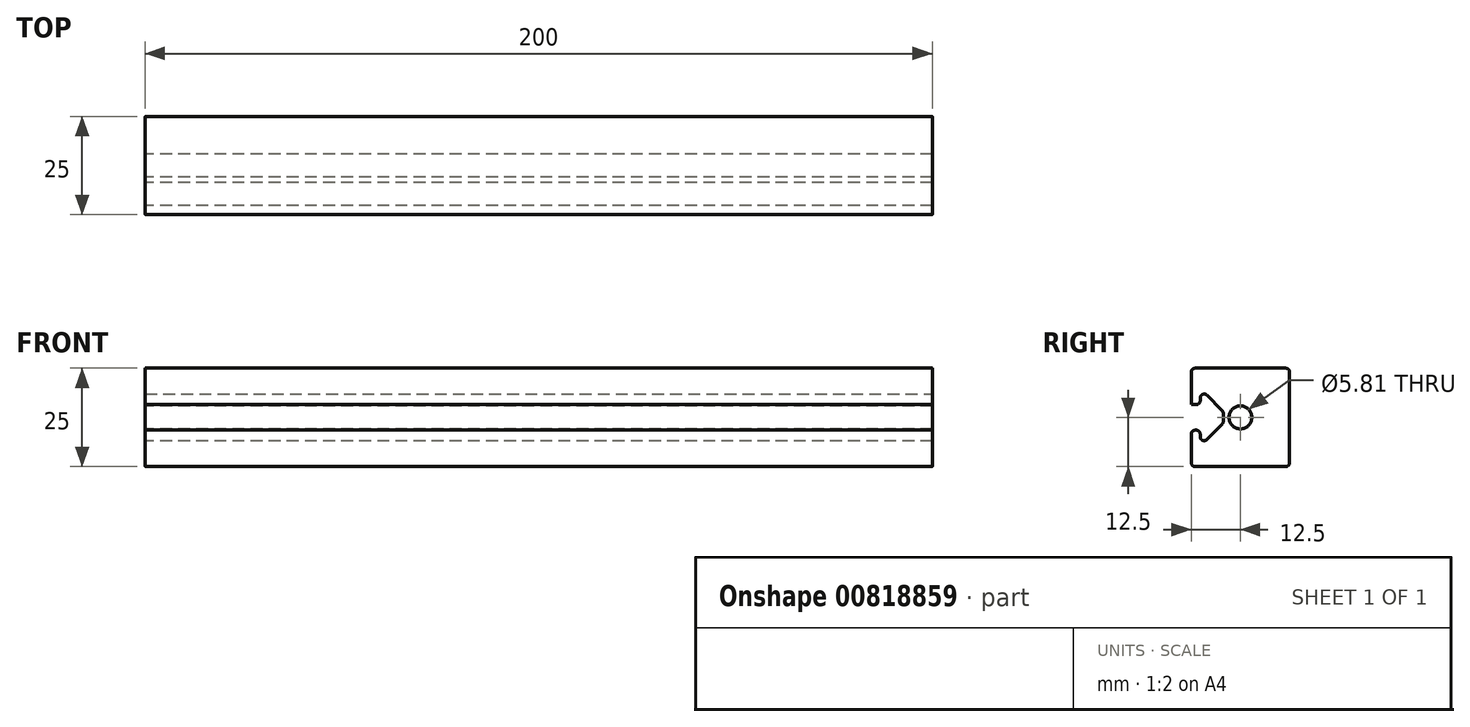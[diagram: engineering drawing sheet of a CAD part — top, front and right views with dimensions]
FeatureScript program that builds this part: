
annotation { "Feature Type Name" : "Feature", "Feature Type Description" : "" }
export const myFeature = defineFeature(function(context is Context, id is Id, definition is map)
    precondition{}
    {
        {
            var Q0;
            Q0=qCreatedBy(makeId("Right.planeOp"),FACE);
            var sketch = newSketch(context, id + "F0", { "sketchPlane" : qUnion([Q0])});
            skLineSegment(sketch, "E0.bottom", {"start": v(-12.5, -25) * mm, "end": v(12.5, -25) * mm});
            skLineSegment(sketch, "E0.top", {"start": v(-12.5, 25) * mm, "end": v(12.5, 25) * mm});
            skLineSegment(sketch, "E0.left", {"start": v(-12.5, -25) * mm, "end": v(-12.5, 25) * mm});
            skLineSegment(sketch, "E0.right", {"start": v(12.5, -25) * mm, "end": v(12.5, 25) * mm});
            skPoint(sketch, "E0.middle", {"position": v(0, 0) * mm});
            skLineSegment(sketch, "E1.bottom", {"start": v(12.5, 15.75) * mm, "end": v(4.38, 15.75) * mm});
            skLineSegment(sketch, "E1.top", {"start": v(12.5, 9.25) * mm, "end": v(4.38, 9.25) * mm});
            skLineSegment(sketch, "E1.left", {"start": v(12.5, 15.75) * mm, "end": v(12.5, 9.25) * mm});
            skLineSegment(sketch, "E1.right", {"start": v(4.38, 15.75) * mm, "end": v(4.38, 9.25) * mm});
            skLineSegment(sketch, "E2.bottom", {"start": v(4.38, 19.85) * mm, "end": v(10.22, 19.85) * mm});
            skLineSegment(sketch, "E2.top", {"start": v(4.38, 5.16) * mm, "end": v(10.22, 5.16) * mm});
            skLineSegment(sketch, "E2.left", {"start": v(4.38, 19.85) * mm, "end": v(4.38, 5.16) * mm});
            skLineSegment(sketch, "E2.right", {"start": v(10.22, 19.85) * mm, "end": v(10.22, 5.16) * mm});
            skPoint(sketch, "E2.middle", {"position": v(7.3, 12.5) * mm});
            skLineSegment(sketch, "E3", {"start": v(7.3, 12.5) * mm, "end": v(12.5, 12.5) * mm});
            skLineSegment(sketch, "E4", {"start": v(0, 25) * mm, "end": v(0, 0) * mm});
            skLineSegment(sketch, "E5", {"start": v(4.38, 14) * mm, "end": v(10.22, 19.85) * mm});
            skLineSegment(sketch, "E6.MirrorCS", {"start": v(4.38, 11) * mm, "end": v(10.22, 5.16) * mm});
            skLineSegment(sketch, "E7", {"start": v(-12.5, 0) * mm, "end": v(12.5, 0) * mm});
            skSolve(sketch);
        }
        {
            var Q0;
            {var subQ5=sQuery(id+"F0.wireOp",EDGE,"E2.right");var subQ6=sQuery(id+"F0.wireOp",EDGE,"E1.bottom");var subQ7=makeQuery(id+"F0.imprint","INTERSECT",VERTEX,{"derivedFrom":[subQ6,subQ5]});Q0=makeQuery(id+"F0.imprint","IMPRINT",FACE,{"disambiguationData":[TD([[makeQuery(id+"F0.imprint","IMPRINT",EDGE,{"disambiguationData":[TD([[subQ7,-1.0]])],"derivedFrom":subQ6}),1.0]])]});}
            var Q1;
            {var subQ0=sQuery(id+"F0.wireOp",EDGE,"E2.right");var subQ1=sQuery(id+"F0.wireOp",EDGE,"E1.top");var subQ2=makeQuery(id+"F0.imprint","INTERSECT",VERTEX,{"derivedFrom":[subQ1,subQ0]});Q1=makeQuery(id+"F0.imprint","IMPRINT",FACE,{"disambiguationData":[TD([[makeQuery(id+"F0.imprint","IMPRINT",EDGE,{"disambiguationData":[TD([[subQ2,-1.0]])],"derivedFrom":subQ1}),1.0]])]});}
            var Q2;
            {var subQ0=sQuery(id+"F0.wireOp",EDGE,"E2.left");var subQ1=sQuery(id+"F0.wireOp",EDGE,"E1.bottom");var subQ2=makeQuery(id+"F0.imprint","INTERSECT",VERTEX,{"derivedFrom":[subQ1,subQ0]});Q2=makeQuery(id+"F0.imprint","IMPRINT",FACE,{"disambiguationData":[TD([[makeQuery(id+"F0.imprint","IMPRINT",EDGE,{"disambiguationData":[TD([[subQ2,1.0]])],"derivedFrom":subQ1}),1.0]])]});}
            var Q3;
            {var subQ5=sQuery(id+"F0.wireOp",EDGE,"E2.bottom");Q3=makeQuery(id+"F0.imprint","IMPRINT",FACE,{"disambiguationData":[TD([[makeQuery(id+"F0.imprint","IMPRINT",EDGE,{"derivedFrom":subQ5}),-1.0]])]});}
            var Q4;
            {var subQ0=sQuery(id+"F0.wireOp",EDGE,"E2.right");var subQ1=sQuery(id+"F0.wireOp",EDGE,"E1.bottom");var subQ2=makeQuery(id+"F0.imprint","INTERSECT",VERTEX,{"derivedFrom":[subQ1,subQ0]});Q4=makeQuery(id+"F0.imprint","IMPRINT",FACE,{"disambiguationData":[TD([[makeQuery(id+"F0.imprint","IMPRINT",EDGE,{"disambiguationData":[TD([[subQ2,-1.0]])],"derivedFrom":subQ1}),-1.0]])]});}
            var Q5;
            {var subQ3=sQuery(id+"F0.wireOp",EDGE,"E2.right");var subQ5=sQuery(id+"F0.wireOp",EDGE,"E3");var subQ7=makeQuery(id+"F0.imprint","INTERSECT",VERTEX,{"derivedFrom":[subQ3,subQ5]});Q5=makeQuery(id+"F0.imprint","IMPRINT",FACE,{"disambiguationData":[TD([[makeQuery(id+"F0.imprint","IMPRINT",EDGE,{"disambiguationData":[TD([[subQ7,1.0]])],"derivedFrom":subQ3}),1.0]])]});}
            var Q6;
            {var subQ3=sQuery(id+"F0.wireOp",EDGE,"E2.right");var subQ5=sQuery(id+"F0.wireOp",EDGE,"E3");var subQ7=makeQuery(id+"F0.imprint","INTERSECT",VERTEX,{"derivedFrom":[subQ3,subQ5]});Q6=makeQuery(id+"F0.imprint","IMPRINT",FACE,{"disambiguationData":[TD([[makeQuery(id+"F0.imprint","IMPRINT",EDGE,{"disambiguationData":[TD([[subQ7,-1.0]])],"derivedFrom":subQ3}),1.0]])]});}
            var Q7;
            {var subQ5=sQuery(id+"F0.wireOp",EDGE,"E2.top");Q7=makeQuery(id+"F0.imprint","IMPRINT",FACE,{"disambiguationData":[TD([[makeQuery(id+"F0.imprint","IMPRINT",EDGE,{"derivedFrom":subQ5}),1.0]])]});}
            var Q8;
            {var subQ0=sQuery(id+"F0.wireOp",EDGE,"E2.left");var subQ1=sQuery(id+"F0.wireOp",EDGE,"E1.top");var subQ2=makeQuery(id+"F0.imprint","INTERSECT",VERTEX,{"derivedFrom":[subQ1,subQ0]});Q8=makeQuery(id+"F0.imprint","IMPRINT",FACE,{"disambiguationData":[TD([[makeQuery(id+"F0.imprint","IMPRINT",EDGE,{"disambiguationData":[TD([[subQ2,1.0]])],"derivedFrom":subQ1}),-1.0]])]});}
            var Q9;
            {var subQ3=sQuery(id+"F0.wireOp",EDGE,"E4");Q9=makeQuery(id+"F0.imprint","IMPRINT",FACE,{"disambiguationData":[TD([[makeQuery(id+"F0.imprint","IMPRINT",EDGE,{"derivedFrom":subQ3}),-1.0]])]});}
            var Q10;
            {var subQ5=sQuery(id+"F0.wireOp",EDGE,"E2.bottom");Q10=makeQuery(id+"F0.imprint","IMPRINT",FACE,{"disambiguationData":[TD([[makeQuery(id+"F0.imprint","IMPRINT",EDGE,{"derivedFrom":subQ5}),1.0]])]});}
            extrude(context, id + "F1", {"entities" : qUnion([Q0, Q1, Q2, Q3, Q4, Q5, Q6, Q7, Q8, Q9, Q10]), "endBound" : BoundingType.SYMMETRIC, "depth" : 200 * mm, "offsetDistance" : 25 * mm});
        }
        {
            var Q0;
            Q0=makeQuery(id+"F1.opExtrude","CAP_FACE",FACE,{"disambiguationData":[OSD([sQuery(id+"F0.wireOp",EDGE,"E0.bottom"),sQuery(id+"F0.wireOp",EDGE,"E0.top"),sQuery(id+"F0.wireOp",EDGE,"E0.left"),sQuery(id+"F0.wireOp",EDGE,"E0.right"),sQuery(id+"F0.wireOp",EDGE,"E1.left")])],"isStart":true});
            var sketch = newSketch(context, id + "F2", { "sketchPlane" : qUnion([Q0])});
            skLineSegment(sketch, "E8.bottom", {"start": v(-12.5, -25) * mm, "end": v(12.5, -25) * mm});
            skLineSegment(sketch, "E8.top", {"start": v(-12.5, 25) * mm, "end": v(12.5, 25) * mm});
            skLineSegment(sketch, "E8.left", {"start": v(-12.5, -25) * mm, "end": v(-12.5, 25) * mm});
            skLineSegment(sketch, "E8.right", {"start": v(12.5, -25) * mm, "end": v(12.5, 25) * mm});
            skPoint(sketch, "E8.middle", {"position": v(0, 0) * mm});
            skLineSegment(sketch, "E9.bottom", {"start": v(12.5, 15.75) * mm, "end": v(4.38, 15.75) * mm});
            skLineSegment(sketch, "E9.top", {"start": v(12.5, 9.25) * mm, "end": v(4.38, 9.25) * mm});
            skLineSegment(sketch, "E9.left", {"start": v(12.5, 15.75) * mm, "end": v(12.5, 9.25) * mm});
            skLineSegment(sketch, "E9.right", {"start": v(4.38, 15.75) * mm, "end": v(4.38, 9.25) * mm});
            skLineSegment(sketch, "E10.bottom", {"start": v(4.38, 19.84) * mm, "end": v(10.22, 19.84) * mm});
            skLineSegment(sketch, "E10.top", {"start": v(4.38, 5.15) * mm, "end": v(10.22, 5.15) * mm});
            skLineSegment(sketch, "E10.left", {"start": v(4.38, 19.84) * mm, "end": v(4.38, 5.15) * mm});
            skLineSegment(sketch, "E10.right", {"start": v(10.22, 19.84) * mm, "end": v(10.22, 5.15) * mm});
            skPoint(sketch, "E10.middle", {"position": v(7.3, 12.5) * mm});
            skLineSegment(sketch, "E11", {"start": v(7.3, 12.5) * mm, "end": v(12.5, 12.5) * mm});
            skLineSegment(sketch, "E12", {"start": v(0, 25) * mm, "end": v(0, 0) * mm});
            skLineSegment(sketch, "E13", {"start": v(4.38, 14) * mm, "end": v(10.22, 19.84) * mm});
            skLineSegment(sketch, "E14.MirrorCS", {"start": v(4.38, 11) * mm, "end": v(10.22, 5.16) * mm});
            skCircle(sketch, "E15", {"center": v(0, 12.5) * mm, "radius": 2.54 * mm});
            skSolve(sketch);
        }
        {
            var Q0;
            {var subQ1=sQuery(id+"F0.wireOp",EDGE,"E0.right");var subQ2=sQuery(id+"F0.wireOp",EDGE,"E0.bottom");var subQ3=makeQuery(id+"FmkFbViQpnCxBQF_1.opFillet","BLEND_EDGE",EDGE,{"blendedFrom":[makeQuery(id+"F1.opExtrude","SWEPT_EDGE",EDGE,{"disambiguationData":[OSD([subQ2,subQ1])]}),makeQuery(id+"F1.opExtrude","CAP_FACE",FACE,{"disambiguationData":[OSD([subQ2,sQuery(id+"F0.wireOp",EDGE,"E0.top"),sQuery(id+"F0.wireOp",EDGE,"E0.left"),subQ1,sQuery(id+"F0.wireOp",EDGE,"E1.left")])],"isStart":true})],"blendedInto":[makeQuery(id+"F1.opExtrude","CAP_FACE",FACE,{"disambiguationData":[OSD([subQ2,sQuery(id+"F0.wireOp",EDGE,"E0.top"),sQuery(id+"F0.wireOp",EDGE,"E0.left"),subQ1,sQuery(id+"F0.wireOp",EDGE,"E1.left")])],"isStart":true})]});Q0=makeQuery(id+"F2.imprint","IMPRINT",FACE,{"disambiguationData":[TD([[makeQuery(id+"F2.imprint","IMPRINT",EDGE,{"derivedFrom":subQ3}),-1.0]])]});}
            var Q1;
            {var subQ5=sQuery(id+"F2.wireOp",EDGE,"E10.right");var subQ6=sQuery(id+"F2.wireOp",EDGE,"E9.bottom");var subQ7=makeQuery(id+"F2.imprint","INTERSECT",VERTEX,{"derivedFrom":[subQ6,subQ5]});Q1=makeQuery(id+"F2.imprint","IMPRINT",FACE,{"disambiguationData":[TD([[makeQuery(id+"F2.imprint","IMPRINT",EDGE,{"disambiguationData":[TD([[subQ7,-1.0]])],"derivedFrom":subQ6}),1.0]])]});}
            var Q2;
            {var subQ0=sQuery(id+"F2.wireOp",EDGE,"E10.right");var subQ1=sQuery(id+"F2.wireOp",EDGE,"E9.bottom");var subQ2=makeQuery(id+"F2.imprint","INTERSECT",VERTEX,{"derivedFrom":[subQ1,subQ0]});Q2=makeQuery(id+"F2.imprint","IMPRINT",FACE,{"disambiguationData":[TD([[makeQuery(id+"F2.imprint","IMPRINT",EDGE,{"disambiguationData":[TD([[subQ2,-1.0]])],"derivedFrom":subQ1}),-1.0]])]});}
            var Q3;
            {var subQ3=sQuery(id+"F2.wireOp",EDGE,"E10.right");var subQ5=sQuery(id+"F2.wireOp",EDGE,"E11");var subQ7=makeQuery(id+"F2.imprint","INTERSECT",VERTEX,{"derivedFrom":[subQ3,subQ5]});Q3=makeQuery(id+"F2.imprint","IMPRINT",FACE,{"disambiguationData":[TD([[makeQuery(id+"F2.imprint","IMPRINT",EDGE,{"disambiguationData":[TD([[subQ7,1.0]])],"derivedFrom":subQ3}),1.0]])]});}
            var Q4;
            {var subQ3=sQuery(id+"F2.wireOp",EDGE,"E10.right");var subQ5=sQuery(id+"F2.wireOp",EDGE,"E11");var subQ7=makeQuery(id+"F2.imprint","INTERSECT",VERTEX,{"derivedFrom":[subQ3,subQ5]});Q4=makeQuery(id+"F2.imprint","IMPRINT",FACE,{"disambiguationData":[TD([[makeQuery(id+"F2.imprint","IMPRINT",EDGE,{"disambiguationData":[TD([[subQ7,-1.0]])],"derivedFrom":subQ3}),1.0]])]});}
            var Q5;
            {var subQ0=sQuery(id+"F2.wireOp",EDGE,"E10.right");var subQ1=sQuery(id+"F2.wireOp",EDGE,"E9.top");var subQ2=makeQuery(id+"F2.imprint","INTERSECT",VERTEX,{"derivedFrom":[subQ1,subQ0]});Q5=makeQuery(id+"F2.imprint","IMPRINT",FACE,{"disambiguationData":[TD([[makeQuery(id+"F2.imprint","IMPRINT",EDGE,{"disambiguationData":[TD([[subQ2,-1.0]])],"derivedFrom":subQ1}),1.0]])]});}
            var Q6;
            Q6=makeQuery(id+"F1.opExtrude","CAP_FACE",FACE,{"disambiguationData":[OSD([sQuery(id+"F0.wireOp",EDGE,"E0.bottom"),sQuery(id+"F0.wireOp",EDGE,"E0.top"),sQuery(id+"F0.wireOp",EDGE,"E0.left"),sQuery(id+"F0.wireOp",EDGE,"E0.right"),sQuery(id+"F0.wireOp",EDGE,"E1.left")])],"isStart":false});
            extrude(context, id + "F3", {"entities" : qUnion([Q0, Q1, Q2, Q3, Q4, Q5]), "operationType" : NewBodyOperationType.REMOVE, "endBound" : BoundingType.UP_TO_NEXT, "oppositeDirection" : true, "depth" : 190.4 * mm, "endBoundEntityFace" : qUnion([Q6]), "offsetDistance" : 25 * mm});
        }
        {
            var Q0;
            Q0=qCreatedBy(makeId("Front.planeOp"),FACE);
            var sketch = newSketch(context, id + "F4", { "sketchPlane" : qUnion([Q0])});
            skLineSegment(sketch, "E16", {"start": v(0, 0) * mm, "end": v(0, 12.5) * mm});
            skLineSegment(sketch, "E17", {"start": v(0, 12.5) * mm, "end": v(-154.88, 12.5) * mm});
            skSolve(sketch);
        }
        {
            var Q0;
            Q0=makeQuery(id+"F3.boolean.opBoolean","COPY",EDGE,{"derivedFrom":makeQuery(id+"F3.opExtrude","SWEPT_EDGE",EDGE,{"disambiguationData":[OSD([sQuery(id+"F2.wireOp",EDGE,"E10.left"),sQuery(id+"F2.wireOp",EDGE,"E13")])]})});
            var Q1;
            Q1=makeQuery(id+"F3.boolean.opBoolean","COPY",EDGE,{"derivedFrom":makeQuery(id+"F3.opExtrude","SWEPT_EDGE",EDGE,{"disambiguationData":[OSD([sQuery(id+"F2.wireOp",EDGE,"E10.left"),sQuery(id+"F2.wireOp",EDGE,"E14.MirrorCS")])]})});
            var Q2;
            Q2=makeQuery(id+"F3.boolean.opBoolean","COPY",EDGE,{"derivedFrom":makeQuery(id+"F3.opExtrude","SWEPT_EDGE",EDGE,{"disambiguationData":[OSD([sQuery(id+"F2.wireOp",EDGE,"E10.bottom"),sQuery(id+"F2.wireOp",EDGE,"E10.right"),sQuery(id+"F2.wireOp",EDGE,"E13")])]})});
            var Q3;
            Q3=makeQuery(id+"F3.boolean.opBoolean","COPY",EDGE,{"derivedFrom":makeQuery(id+"F3.opExtrude","SWEPT_EDGE",EDGE,{"disambiguationData":[OSD([sQuery(id+"F2.wireOp",EDGE,"E9.bottom"),sQuery(id+"F2.wireOp",EDGE,"E10.right")])]})});
            var Q4;
            Q4=makeQuery(id+"F3.boolean.opBoolean","COPY",EDGE,{"derivedFrom":makeQuery(id+"F3.opExtrude","SWEPT_EDGE",EDGE,{"disambiguationData":[OSD([sQuery(id+"F2.wireOp",EDGE,"E8.right"),sQuery(id+"F2.wireOp",EDGE,"E9.bottom"),sQuery(id+"F2.wireOp",EDGE,"E9.left")])]})});
            var Q5;
            Q5=makeQuery(id+"F3.boolean.opBoolean","COPY",EDGE,{"derivedFrom":makeQuery(id+"F3.opExtrude","SWEPT_EDGE",EDGE,{"disambiguationData":[OSD([sQuery(id+"F2.wireOp",EDGE,"E8.right"),sQuery(id+"F2.wireOp",EDGE,"E9.top"),sQuery(id+"F2.wireOp",EDGE,"E9.left")])]})});
            var Q6;
            Q6=makeQuery(id+"F3.boolean.opBoolean","COPY",EDGE,{"derivedFrom":makeQuery(id+"F3.opExtrude","SWEPT_EDGE",EDGE,{"disambiguationData":[OSD([sQuery(id+"F2.wireOp",EDGE,"E9.top"),sQuery(id+"F2.wireOp",EDGE,"E10.right")])]})});
            var Q7;
            Q7=makeQuery(id+"F3.boolean.opBoolean","COPY",EDGE,{"derivedFrom":makeQuery(id+"F3.opExtrude","SWEPT_EDGE",EDGE,{"disambiguationData":[OSD([sQuery(id+"F2.wireOp",EDGE,"E10.top"),sQuery(id+"F2.wireOp",EDGE,"E10.right"),sQuery(id+"F2.wireOp",EDGE,"E14.MirrorCS")])]})});
            var Q8;
            Q8=makeQuery(id+"F1.opExtrude","SWEPT_EDGE",EDGE,{"disambiguationData":[OSD([sQuery(id+"F0.wireOp",EDGE,"E0.top"),sQuery(id+"F0.wireOp",EDGE,"E0.right")])]});
            var Q9;
            Q9=makeQuery(id+"F1.opExtrude","SWEPT_EDGE",EDGE,{"disambiguationData":[OSD([sQuery(id+"F0.wireOp",EDGE,"E0.top"),sQuery(id+"F0.wireOp",EDGE,"E0.left")])]});
            var Q10;
            Q10=makeQuery(id+"F1.opExtrude","SWEPT_EDGE",EDGE,{"disambiguationData":[OSD([sQuery(id+"F0.wireOp",EDGE,"E0.left"),sQuery(id+"F0.wireOp",EDGE,"E7")])]});
            var Q11;
            Q11=makeQuery(id+"F1.opExtrude","SWEPT_EDGE",EDGE,{"disambiguationData":[OSD([sQuery(id+"F0.wireOp",EDGE,"E0.right"),sQuery(id+"F0.wireOp",EDGE,"E7")])]});
            fillet(context, id + "F5", {"entities" : qUnion([Q0, Q1, Q2, Q3, Q4, Q5, Q6, Q7, Q8, Q9, Q10, Q11]), "radius" : 1 * mm, "tangentPropagation" : true, "allowEdgeOverflow" : false});
        }
        {
            var Q0;
            Q0=makeQuery(id+"F1.opExtrude","CAP_FACE",FACE,{"disambiguationData":[OSD([sQuery(id+"F0.wireOp",EDGE,"E0.bottom"),sQuery(id+"F0.wireOp",EDGE,"E0.top"),sQuery(id+"F0.wireOp",EDGE,"E0.left"),sQuery(id+"F0.wireOp",EDGE,"E0.right"),sQuery(id+"F0.wireOp",EDGE,"E1.left")])],"isStart":true});
            var sketch = newSketch(context, id + "F6", { "sketchPlane" : qUnion([Q0])});
            skCircle(sketch, "E18", {"center": v(0, 0) * mm, "radius": 8 * mm});
            skCircle(sketch, "E19", {"center": v(0, 12.5) * mm, "radius": 2.5 * mm});
            skCircle(sketch, "E20", {"center": v(0, -12.5) * mm, "radius": 2.5 * mm});
            skSolve(sketch);
        }
        {
            var Q0;
            Q0=makeQuery(id+"F1.opExtrude","CAP_FACE",FACE,{"disambiguationData":[OSD([sQuery(id+"F0.wireOp",EDGE,"E0.top"),sQuery(id+"F0.wireOp",EDGE,"E0.left"),sQuery(id+"F0.wireOp",EDGE,"E0.right"),sQuery(id+"F0.wireOp",EDGE,"E1.left"),sQuery(id+"F0.wireOp",EDGE,"E7")])],"isStart":true});
            var sketch = newSketch(context, id + "F7", { "sketchPlane" : qUnion([Q0])});
            skCircle(sketch, "E21", {"center": v(0, 12.5) * mm, "radius": 2.9 * mm});
            skLineSegment(sketch, "E22", {"start": v(4.38, 12.5) * mm, "end": v(2.9, 12.5) * mm});
            skLineSegment(sketch, "E23", {"start": v(-4.38, 12.5) * mm, "end": v(0, 16.88) * mm});
            skLineSegment(sketch, "E24", {"start": v(0, 16.88) * mm, "end": v(0, 15.4) * mm});
            skLineSegment(sketch, "E25.trimOffspring", {"start": v(0, 9.6) * mm, "end": v(0, 8.12) * mm});
            skLineSegment(sketch, "E26.trimOffspring", {"start": v(-2.9, 12.5) * mm, "end": v(-4.38, 12.5) * mm});
            skSolve(sketch);
        }
        {
            var Q0;
            {var subQ0=sQuery(id+"F7.wireOp",EDGE,"E21");var subQ1=makeQuery(id+"F7.imprint","INTERSECT",VERTEX,{"derivedFrom":[subQ0,sQuery(id+"F7.wireOp",EDGE,"E22")]});Q0=makeQuery(id+"F7.imprint","IMPRINT",FACE,{"disambiguationData":[TD([[makeQuery(id+"F7.imprint","IMPRINT",EDGE,{"disambiguationData":[TD([[subQ1,-1.0]])],"derivedFrom":subQ0}),1.0]])]});}
            extrude(context, id + "F8", {"entities" : qUnion([Q0]), "operationType" : NewBodyOperationType.REMOVE, "endBound" : BoundingType.UP_TO_NEXT, "oppositeDirection" : true, "depth" : 25 * mm, "offsetDistance" : 25 * mm});
        }
    });
